FCSTD DOCUMENT  (FreeCAD 1.0R39319 (Git))
Label: ASSEMBLY-CANVAS
License: All rights reserved
LicenseURL: https://en.wikipedia.org/wiki/All_rights_reserved
objects: App::Link×9, Part::FeaturePython×7, App::DocumentObjectGroup×3, PartDesign::CoordinateSystem×2, App::FeaturePython×1, Sketcher::SketchObject×1, App::Part×1
note: 11 computed .brp shape members not serialized (recipe doc carries the construction recipe); baked Part::Feature solids carry a one-line shape summary decoded from their .brp
EXTERNAL_REF file=../Design/PLASTIC-CANVAS/PLASTIC-CANVAS.FCStd obj=LCS_Origin
EXTERNAL_REF file=../Design/PLASTIC-CANVAS/PLASTIC-CANVAS.FCStd obj=Body002
EXTERNAL_REF file=../Design/PLASTIC-CANVAS/PLASTIC-CANVAS.FCStd obj=CircleAxis_1
EXTERNAL_REF file=../Design/RUBBER-FOOT/RUBBER-FOOT.FCStd obj=CircleAxis_2
EXTERNAL_REF file=../Design/RUBBER-FOOT/RUBBER-FOOT.FCStd obj=Body
EXTERNAL_REF file=../Design/INSERT-M1.6x2.5x3/INSERT-M1.6x2.5x3.FCStd obj=CircleAxis_1
EXTERNAL_REF file=../Design/PLASTIC-CANVAS/PLASTIC-CANVAS.FCStd obj=CircleAxis_3
EXTERNAL_REF file=../Design/INSERT-M1.6x2.5x3/INSERT-M1.6x2.5x3.FCStd obj=Body
EXTERNAL_REF file=../Design/INSERT-M1.6x2.5x4/INSERT-M1.6x2.5x4.FCStd obj=Plane_1
EXTERNAL_REF file=../Design/PLASTIC-CANVAS/PLASTIC-CANVAS.FCStd obj=CircleAxis_4
EXTERNAL_REF file=../Design/INSERT-M1.6x2.5x4/INSERT-M1.6x2.5x4.FCStd obj=Body
EXTERNAL_REF file=../Design/MAGNET-D3x14/MAGNET-D3x14.FCStd obj=LCS_1
EXTERNAL_REF file=../Design/PLASTIC-CANVAS/PLASTIC-CANVAS.FCStd obj=LCS_3
EXTERNAL_REF file=../Design/MAGNET-D3x14/MAGNET-D3x14.FCStd obj=Body001
EXTERNAL_REF file=../Design/PLASTIC-CANVAS/PLASTIC-CANVAS.FCStd obj=LCS_4
EXTERNAL_REF file=../Design/MAGNET-SQ3/MAGNET-SQ3.FCStd obj=Axis_2
EXTERNAL_REF file=../Design/PLASTIC-CANVAS/PLASTIC-CANVAS.FCStd obj=Axis_2
EXTERNAL_REF file=../Design/MAGNET-SQ3/MAGNET-SQ3.FCStd obj=Body002
EXTERNAL_REF file=PCBAs/PCBA-INTERFACE.FCStd obj=CircleAxis_1
EXTERNAL_REF file=../Design/PLASTIC-CANVAS/PLASTIC-CANVAS.FCStd obj=Axis_3
EXTERNAL_REF file=PCBAs/PCBA-INTERFACE.FCStd obj=PCBA_INTERFACE_3D_1
EXTERNAL_REF file=../Design/PLASTIC-CANVAS/PLASTIC-CANVAS.FCStd obj=LCS_5
EXTERNAL_REF file=../Design/PLASTIC-MAPMODE/PLASTIC-MAPMODE.FCStd obj=LCS_1
EXTERNAL_REF file=../Design/PLASTIC-MAPMODE/PLASTIC-MAPMODE.FCStd obj=Body

FEATURE [App::DocumentObjectGroup] Parts
FEATURE [PartDesign::CoordinateSystem] LCS_Origin
  AttacherType = Attacher::AttachEngine3D
  AttachmentSupport = -> [X_Axis]
  MapMode = 2
FEATURE [App::DocumentObjectGroup] Constraints
FEATURE [App::FeaturePython] Variables  # WARN: FeaturePython — macro-defined, semantics opaque (R4)
  Type = App::PropertyContainer
FEATURE [App::DocumentObjectGroup] Configurations
FEATURE [App::Link] PLASTIC_CANVAS  label="PLASTIC-CANVAS"
  AttachedBy = #LCS_Origin
  AttachedTo = Parent Assembly#LCS_Origin
  LinkedObject = -> <external ../Design/PLASTIC-CANVAS/PLASTIC-CANVAS.FCStd>#Body002
  SolverId = Asm4EE
  expr: Placement = LCS_Origin.Placement * AttachmentOffset * PLASTIC_CANVAS#LCS_Origin.Placement ^ -1
FEATURE [App::Link] RUBBER_FOOT  label="RUBBER-FOOT"
  AttachedBy = #CircleAxis_2
  AttachedTo = PLASTIC_CANVAS#CircleAxis_1
  LinkPlacement = pos=(-33.85,38,-16) rot=(0,0,1;0rad)
  LinkedObject = -> <external ../Design/RUBBER-FOOT/RUBBER-FOOT.FCStd>#Body
  Placement = pos=(-33.85,38,-16) rot=(0,0,1;0rad)
  SolverId = Asm4EE
  expr: Placement = PLASTIC_CANVAS.Placement * PLASTIC_CANVAS#CircleAxis_1.Placement * AttachmentOffset * RUBBER_FOOT#CircleAxis_2.Placement ^ -1
FEATURE [Part::FeaturePython] Circular_RUBBER_FOOT  label="Circular_RUBBER-FOOT"  # Draft array (typed FeaturePython)
  AngleStep = 90
  ArrayType = Circular Array
  Axis = -> LCS_Origin [Z]
  Count = 4
  Index = 1
  PlacementList = 4 placements: [(-33.85,38,-16),(-38,-33.85,-16),(33.85,-38,-16),(38,33.85,-16)]
  Placer = pos=(0,0,0) rot=(0,0,1;4.71239rad)
  ScaleList = (4) [(1,1,1),(1,1,1),(1,1,1),(1,1,1)]
  Scaler = 1
  ShowElement = false
  SourceObject = -> RUBBER_FOOT
  expr: .Placer.Rotation.Angle = AngleStep * Index
  expr: AngleStep = 360 / Count
FEATURE [App::Link] INSERT_M1_6x2_5x3  label="INSERT-M1.6x2.5x3"
  AttachedBy = #CircleAxis_1
  AttachedTo = PLASTIC_CANVAS#CircleAxis_3
  AttachmentOffset = pos=(0,0,0) rot=(1,0,0;3.14159rad)
  LinkPlacement = pos=(-26.67,26.67,-14) rot=(1,0,0;3.14159rad)
  LinkedObject = -> <external ../Design/INSERT-M1.6x2.5x3/INSERT-M1.6x2.5x3.FCStd>#Body
  Placement = pos=(-26.67,26.67,-14) rot=(1,0,0;3.14159rad)
  SolverId = Asm4EE
  expr: Placement = PLASTIC_CANVAS.Placement * PLASTIC_CANVAS#CircleAxis_3.Placement * AttachmentOffset * INSERT_M1_6x2_5x3#CircleAxis_1.Placement ^ -1
FEATURE [Part::FeaturePython] Circular_INSERT_M1_6x2_5x3  label="Circular_INSERT-M1.6x2.5x3"  # Draft array (typed FeaturePython)
  AngleStep = 90
  ArrayType = Circular Array
  Axis = -> LCS_Origin [Z]
  Count = 4
  Index = 1
  PlacementList = 4 placements: [(-26.67,26.67,-14),(-26.67,-26.67,-14),(26.67,-26.67,-14),(26.67,26.67,-14)]
  Placer = pos=(0,0,0) rot=(0,0,1;4.71239rad)
  ScaleList = (4) [(1,1,1),(1,1,1),(1,1,1),(1,1,1)]
  Scaler = 1
  ShowElement = false
  SourceObject = -> INSERT_M1_6x2_5x3
  expr: .Placer.Rotation.Angle = AngleStep * Index
  expr: AngleStep = 360 / Count
FEATURE [App::Link] INSERT_M1_6x2_5x4  label="INSERT-M1.6x2.5x4"
  AttachedBy = #Plane_1
  AttachedTo = PLASTIC_CANVAS#CircleAxis_4
  AttachmentOffset = pos=(0,0,0) rot=(1,0,0;3.14159rad)
  LinkPlacement = pos=(-50,50,-13.5) rot=(1,0,0;3.14159rad)
  LinkedObject = -> <external ../Design/INSERT-M1.6x2.5x4/INSERT-M1.6x2.5x4.FCStd>#Body
  Placement = pos=(-50,50,-13.5) rot=(1,0,0;3.14159rad)
  SolverId = Asm4EE
  expr: Placement = PLASTIC_CANVAS.Placement * PLASTIC_CANVAS#CircleAxis_4.Placement * AttachmentOffset * INSERT_M1_6x2_5x4#Plane_1.Placement ^ -1
FEATURE [Part::FeaturePython] Circular_INSERT_M1_6x2_5x4  label="Circular_INSERT-M1.6x2.5x4"  # Draft array (typed FeaturePython)
  AngleStep = 90
  ArrayType = Circular Array
  Axis = -> LCS_Origin [Z]
  Count = 4
  Index = 1
  PlacementList = 4 placements: [(-50,50,-13.5),(-50,-50,-13.5),(50,-50,-13.5),(50,50,-13.5)]
  Placer = pos=(0,0,0) rot=(0,0,1;4.71239rad)
  ScaleList = (4) [(1,1,1),(1,1,1),(1,1,1),(1,1,1)]
  Scaler = 1
  ShowElement = false
  SourceObject = -> INSERT_M1_6x2_5x4
  expr: .Placer.Rotation.Angle = AngleStep * Index
  expr: AngleStep = 360 / Count
FEATURE [App::Link] MAGNET_D3x14  label="MAGNET-D3x14"
  AttachedBy = #LCS_1
  AttachedTo = PLASTIC_CANVAS#LCS_3
  AttachmentOffset = pos=(0,0,0.25) rot=(0.71,-0.71,0;3.14159rad)
  LinkPlacement = pos=(-47,51.7,-13.25) rot=(0,0,-1;4.00114rad)
  LinkedObject = -> <external ../Design/MAGNET-D3x14/MAGNET-D3x14.FCStd>#Body001
  Placement = pos=(-47,51.7,-13.25) rot=(0,0,-1;4.00114rad)
  SolverId = Asm4EE
  expr: Placement = PLASTIC_CANVAS.Placement * PLASTIC_CANVAS#LCS_3.Placement * AttachmentOffset * MAGNET_D3x14#LCS_1.Placement ^ -1
FEATURE [App::Link] MAGNET_D3x015  label="MAGNET-D3x015"
  AttachedBy = #LCS_1
  AttachedTo = PLASTIC_CANVAS#LCS_4
  AttachmentOffset = pos=(0,0,0.25) rot=(1,0,0;3.14159rad)
  LinkPlacement = pos=(-51.7,47,-13.25) rot=(0,0,1;2.28204rad)
  LinkedObject = -> <external ../Design/MAGNET-D3x14/MAGNET-D3x14.FCStd>#Body001
  Placement = pos=(-51.7,47,-13.25) rot=(0,0,1;2.28204rad)
  SolverId = Asm4EE
  expr: Placement = PLASTIC_CANVAS.Placement * PLASTIC_CANVAS#LCS_4.Placement * AttachmentOffset * MAGNET_D3x14#LCS_1.Placement ^ -1
FEATURE [Part::FeaturePython] Circular_MAGNET_D3x14  label="Circular_MAGNET-D3x14"  # Draft array (typed FeaturePython)
  AngleStep = 90
  ArrayType = Circular Array
  Axis = -> LCS_Origin [Z]
  Count = 4
  Index = 1
  PlacementList = 4 placements: [(-47,51.7,-13.25),(-51.7,-47,-13.25),(47,-51.7,-13.25),(51.7,47,-13.25)]
  Placer = pos=(0,0,0) rot=(0,0,1;4.71239rad)
  ScaleList = (4) [(1,1,1),(1,1,1),(1,1,1),(1,1,1)]
  Scaler = 1
  ShowElement = false
  SourceObject = -> MAGNET_D3x14
  expr: .Placer.Rotation.Angle = AngleStep * Index
  expr: AngleStep = 360 / Count
FEATURE [Part::FeaturePython] Circular_MAGNET_D3x015  label="Circular_MAGNET-D3x015"  # Draft array (typed FeaturePython)
  AngleStep = 90
  ArrayType = Circular Array
  Axis = -> LCS_Origin [Z]
  Count = 4
  Index = 1
  PlacementList = 4 placements: [(-51.7,47,-13.25),(-47,-51.7,-13.25),(51.7,-47,-13.25),(47,51.7,-13.25)]
  Placer = pos=(0,0,0) rot=(0,0,1;4.71239rad)
  ScaleList = (4) [(1,1,1),(1,1,1),(1,1,1),(1,1,1)]
  Scaler = 1
  ShowElement = false
  SourceObject = -> MAGNET_D3x015
  expr: .Placer.Rotation.Angle = AngleStep * Index
  expr: AngleStep = 360 / Count
FEATURE [App::Link] MAGNET_SQ3  label="MAGNET-SQ3"
  AttachedBy = #Axis_2
  AttachedTo = PLASTIC_CANVAS#Axis_2
  AttachmentOffset = pos=(-0.2,0,16.18) rot=(0,1,0;3.14159rad)
  LinkPlacement = pos=(16.18,50.12,-13.25) rot=(0,0,1;3.14159rad)
  LinkedObject = -> <external ../Design/MAGNET-SQ3/MAGNET-SQ3.FCStd>#Body002
  Placement = pos=(16.18,50.12,-13.25) rot=(0,0,1;3.14159rad)
  SolverId = Asm4EE
  expr: Placement = PLASTIC_CANVAS.Placement * PLASTIC_CANVAS#Axis_2.Placement * AttachmentOffset * MAGNET_SQ3#Axis_2.Placement ^ -1
FEATURE [Part::FeaturePython] Circular_MAGNET_SQ3  label="Circular_MAGNET-SQ3"  # Draft array (typed FeaturePython)
  AngleStep = 90
  ArrayType = Circular Array
  Axis = -> LCS_Origin [Z]
  Count = 4
  Index = 1
  PlacementList = 4 placements: [(16.18,50.12,-13.25),(-50.12,16.18,-13.25),(-16.18,-50.12,-13.25),(50.12,-16.18,-13.25)]
  Placer = pos=(0,0,0) rot=(0,0,1;4.71239rad)
  ScaleList = (4) [(1,1,1),(1,1,1),(1,1,1),(1,1,1)]
  Scaler = 1
  ShowElement = false
  SourceObject = -> MAGNET_SQ3
  expr: .Placer.Rotation.Angle = AngleStep * Index
  expr: AngleStep = 360 / Count
FEATURE [App::Link] PCBA_INTERFACE_3D_1  label="PCBA-INTERFACE-3D 1"
  AttachedBy = #CircleAxis_1
  AttachedTo = PLASTIC_CANVAS#Axis_3
  AttachmentOffset = pos=(0,0,0) rot=(0,0,1.00409;4.71239rad)
  LinkPlacement = pos=(-100.032,53.1114,100.044) rot=(-1,0.000152,-0.000155;4.72984rad)
  LinkedObject = -> <external PCBAs/PCBA-INTERFACE.FCStd>#PCBA_INTERFACE_3D_1
  Placement = pos=(-100.032,53.1114,100.044) rot=(-1,0.000152,-0.000155;4.72984rad)
  SolverId = Asm4EE
  expr: Placement = PLASTIC_CANVAS.Placement * PLASTIC_CANVAS#Axis_3.Placement * AttachmentOffset * PCBA_INTERFACE#CircleAxis_1.Placement ^ -1
FEATURE [Part::FeaturePython] Circular_PCBA_INTERFACE_3D_1  label="Circular_PCBA-INTERFACE-3D 1"  # Draft array (typed FeaturePython)
  AngleStep = 90
  ArrayType = Circular Array
  Axis = -> LCS_Origin [Z]
  Count = 4
  Index = 1
  PlacementList = 4 placements: [(-100.032,53.1114,100.044),(-53.1114,-100.032,100.044),(100.032,-53.1114,100.044),(53.1114,100.032,100.044)]
  Placer = pos=(0,0,0) rot=(0,0,1;4.71239rad)
  ScaleList = (4) [(1,1,1),(1,1,1),(1,1,1),(1,1,1)]
  Scaler = 1
  ShowElement = false
  SourceObject = -> PCBA_INTERFACE_3D_1
  expr: .Placer.Rotation.Angle = AngleStep * Index
  expr: AngleStep = 360 / Count
FEATURE [PartDesign::CoordinateSystem] LCS_1
  AttacherType = Attacher::AttachEngine3D
FEATURE [Sketcher::SketchObject] Sketch_1
  ArcFitTolerance = 1e-06
  AttachmentSupport = -> [XZ_Plane]
  FullyConstrained = true
  MakeInternals = false
  MapMode = 5
  Placement = pos=(0,0,0) rot=(1,0,0;1.5708rad)
FEATURE [App::Link] PLASTIC_MAPMODE  label="PLASTIC-MAPMODE"
  AttachedBy = #LCS_1
  AttachedTo = PLASTIC_CANVAS#LCS_5
  AttachmentOffset = pos=(0,0,0.8) rot=(0,0,1;0rad)
  LinkPlacement = pos=(-2.147e-13,-48.5772,-6.3955) rot=(-0.579059,-0.573917,-0.579059;4.18363rad)
  LinkedObject = -> <external ../Design/PLASTIC-MAPMODE/PLASTIC-MAPMODE.FCStd>#Body
  Placement = pos=(-2.147e-13,-48.5772,-6.3955) rot=(-0.579059,-0.573917,-0.579059;4.18363rad)
  SolverId = Asm4EE
  expr: Placement = PLASTIC_CANVAS.Placement * PLASTIC_CANVAS#LCS_5.Placement * AttachmentOffset * PLASTIC_MAPMODE#LCS_1.Placement ^ -1
FEATURE [App::Part] Assembly
  AssemblyType = Part::Link
  Group = -> [LCS_Origin,Constraints,Variables,Configurations,PLASTIC_CANVAS,RUBBER_FOOT,Circular_RUBBER_FOOT,INSERT_M1_6x2_5x3,Circular_INSERT_M1_6x2_5x3,INSERT_M1_6x2_5x4,Circular_INSERT_M1_6x2_5x4,MAGNET_D3x14,MAGNET_D3x015,Circular_MAGNET_D3x14,Circular_MAGNET_D3x015,MAGNET_SQ3,Circular_MAGNET_SQ3,PCBA_INTERFACE_3D_1,Circular_PCBA_INTERFACE_3D_1,LCS_1,Sketch_1,PLASTIC_MAPMODE]
  Origin = -> Origin
  Type = Assembly

RESOLVED EXTERNAL PARTS (link-assembly join: the EXTERNAL_REF files above that resolve inside this repo's crawl, each included once):
---- part ../Design/INSERT-M1.6x2.5x3/INSERT-M1.6x2.5x3.FCStd = doc fcstd_65dee94a8ec8 ----
FCSTD DOCUMENT  (FreeCAD 1.0R39319 (Git))
Label: INSERT-M1.6x2.5x3
License: All rights reserved
LicenseURL: https://en.wikipedia.org/wiki/All_rights_reserved
objects: Sketcher::SketchObject×4, PartDesign::Pad×2, PartDesign::Plane×2, PartDesign::PolarPattern×1, PartDesign::Groove×1, PartDesign::AdditiveHelix×1, PartDesign::Line×1, PartDesign::Body×1
note: 26 computed .brp shape members not serialized (recipe doc carries the construction recipe); baked Part::Feature solids carry a one-line shape summary decoded from their .brp

FEATURE [Sketcher::SketchObject] Sketch
  ArcFitTolerance = 0
  AttachmentSupport = -> [XY_Plane]
  FullyConstrained = true
  MakeInternals = false
  MapMode = 5
  sketch-geometry (2):
    g0: Circle CenterX=0 CenterY=0 CenterZ=0 NormalX=0 NormalY=0 NormalZ=1 AngleXU=0 Radius=0.8
    g1: Circle CenterX=0 CenterY=0 CenterZ=0 NormalX=0 NormalY=0 NormalZ=1 AngleXU=0 Radius=1
  constraints (4):
    c: Coincident(g0,g-1)
    c: Coincident(g1,g0)
    c: Diameter(g0) = 1.6
    c: Diameter(g1) = 2
FEATURE [PartDesign::Pad] Pad
  Direction = (0,0,1)
  Length = 3
  Length2 = 10
  Midplane = true
  Profile = -> Sketch
  ReferenceAxis = -> Sketch [N_Axis]
  Suppressed = false
  Type = 0
FEATURE [Sketcher::SketchObject] Sketch001
  ArcFitTolerance = 0
  AttachmentSupport = -> [XZ_Plane]
  FullyConstrained = true
  MakeInternals = false
  MapMode = 5
  Placement = pos=(0,0,0) rot=(1,0,0;1.5708rad)
  sketch-geometry (5):
    g0: LineSegment StartX=-0.8 StartY=-1.4 StartZ=0 EndX=-0.6105 EndY=-1.29059 EndZ=0
    g1: LineSegment StartX=-0.6105 StartY=-1.29059 StartZ=0 EndX=-0.8 EndY=-1.18118 EndZ=0
    g2: LineSegment StartX=-0.8 StartY=-1.4 StartZ=0 EndX=-0.9 EndY=-1.4 EndZ=0
    g3: LineSegment StartX=-0.9 StartY=-1.4 StartZ=0 EndX=-0.9 EndY=-1.18118 EndZ=0
    g4: LineSegment StartX=-0.8 StartY=-1.18118 StartZ=0 EndX=-0.9 EndY=-1.18118 EndZ=0
  constraints (15):
    c: Coincident(g1,g0)
    c: Vertical(g0,g1)
    c: Equal(g1,g0)
    c: Angle(g1,g0) = 1.0472
    c: Coincident(g2,g0)
    c: Horizontal(g2)
    c: Coincident(g3,g2)
    c: Vertical(g3)
    c: Coincident(g4,g1)
    c: Horizontal(g4)
    c: Coincident(g3,g4)
    c: Distance(g4) = 0.1
    c: Distance(g0,g-2) = 0.6105
    c: DistanceX(g1,g-1) = 0.8
    c: DistanceY(g0,g-1) = 1.4
FEATURE [PartDesign::Plane] DatumPlane
  AttachmentOffset = pos=(0,0,1.5) rot=(0,0,1;0rad)
  AttachmentSupport = -> [XY_Plane]
  Length = 60
  MapMode = 5
  Placement = pos=(0,0,1.5) rot=(0,0,1;0rad)
  ResizeMode = 0
  Width = 60
FEATURE [Sketcher::SketchObject] Sketch002
  ArcFitTolerance = 0
  AttachmentSupport = -> [DatumPlane]
  FullyConstrained = true
  MakeInternals = false
  MapMode = 5
  Placement = pos=(0,0,1.5) rot=(0,0,1;0rad)
  sketch-geometry (2):
    g0: ArcOfCircle CenterX=0 CenterY=0 CenterZ=0 NormalX=0 NormalY=0 NormalZ=1 AngleXU=0 Radius=0.85 StartAngle=1.35344 EndAngle=1.78815
    g1: ArcOfCircle CenterX=0 CenterY=1 CenterZ=0 NormalX=0 NormalY=0 NormalZ=1 AngleXU=0 Radius=0.25 StartAngle=5.53542 EndAngle=10.1725
  constraints (7):
    c: Diameter(g0) = 1.7
    c: PointOnObject(g1,g-2)
    c: Diameter(g1) = 0.5
    c: Coincident(g0,g1)
    c: Coincident(g0,g1)
    c: DistanceY(g0,g1) = 1
    c: Coincident(g0,g-1)
FEATURE [PartDesign::Pad] Pad001
  BaseFeature = -> Pad
  Direction = (0,0,1)
  Length = 3
  Length2 = 10
  Profile = -> Sketch002
  ReferenceAxis = -> Sketch002 [N_Axis]
  Refine = true
  Reversed = true
  Suppressed = false
  Type = 0
FEATURE [PartDesign::PolarPattern] PolarPattern
  Angle = 360
  Axis = -> Sketch002 [N_Axis]
  BaseFeature = -> Pad001
  Mode = 0
  Occurrences = 21
  Offset = 120
  Originals = -> [Pad001]
  Refine = true
  Suppressed = false
  TransformMode = 0
FEATURE [Sketcher::SketchObject] Sketch003
  ArcFitTolerance = 0
  AttachmentSupport = -> [XZ_Plane]
  FullyConstrained = true
  MakeInternals = false
  MapMode = 5
  Placement = pos=(0,0,0) rot=(1,0,0;1.5708rad)
  sketch-geometry (5):
    g0: LineSegment StartX=-1 StartY=0.5 StartZ=0 EndX=-1 EndY=-0.5 EndZ=0
    g1: LineSegment [constr] StartX=0 StartY=0 StartZ=0 EndX=-1 EndY=0 EndZ=0
    g2: LineSegment StartX=-1 StartY=0.5 StartZ=0 EndX=-1.6 EndY=0.5 EndZ=0
    g3: LineSegment StartX=-1.6 StartY=0.5 StartZ=0 EndX=-1.6 EndY=-0.5 EndZ=0
    g4: LineSegment StartX=-1 StartY=-0.5 StartZ=0 EndX=-1.6 EndY=-0.5 EndZ=0
  constraints (14):
    c: Coincident(g1,g-1)
    c: Horizontal(g1)
    c: Symmetric(g0,g0,g1)
    c: DistanceY(g0,g0) = 1
    c: Coincident(g2,g0)
    c: Horizontal(g2)
    c: Coincident(g3,g2)
    c: Vertical(g3)
    c: Coincident(g4,g0)
    c: Horizontal(g4)
    c: Coincident(g3,g4)
    c: DistanceX(g2,g2) = 0.6
    c: Vertical(g0)
    c: DistanceX(g1,g1) = 1
FEATURE [PartDesign::Groove] Groove
  Angle = 360
  Angle2 = 60
  Axis = (0,2e-16,1)
  Base = (0,0,0)
  BaseFeature = -> PolarPattern
  Profile = -> Sketch003
  ReferenceAxis = -> Sketch003 [V_Axis]
  Reversed = true
  Suppressed = false
  Type = 0
FEATURE [PartDesign::AdditiveHelix] AdditiveHelix
  Angle = 0
  Axis = (0,2e-16,1)
  Base = (0,0,0)
  BaseFeature = -> Groove
  Growth = 0
  HasBeenEdited = true
  Height = 2.6
  LeftHanded = false
  Mode = 0
  Outside = false
  Pitch = 0.35
  Profile = -> Sketch001
  ReferenceAxis = -> Sketch001 [V_Axis]
  Refine = true
  Suppressed = false
  Tolerance = 0.1
  Turns = 7.42857
FEATURE [PartDesign::Plane] Plane_1
  AttachmentSupport = -> [AdditiveHelix]
  Length = 100
  MapMode = 5
  Placement = pos=(0,0,1.5) rot=(0,0,1;0rad)
  ResizeMode = 1
  Width = 100
FEATURE [PartDesign::Line] CircleAxis_1
  AttacherType = Attacher::AttachEngineLine
  AttachmentSupport = -> [AdditiveHelix]
  Length = 4.50902
  MapMode = 19
  Placement = pos=(-1e-16,0,1.5) rot=(0,0,1;0rad)
  ResizeMode = 1
FEATURE [PartDesign::Body] Body  label="INSERT-M1.6x2.5x3"
  AllowCompound = false
  Group = -> [Sketch,Pad,Sketch001,DatumPlane,Sketch002,Pad001,PolarPattern,Sketch003,Groove,AdditiveHelix,Plane_1,CircleAxis_1]
  Origin = -> Origin
  Tip = -> AdditiveHelix
---- part ../Design/INSERT-M1.6x2.5x4/INSERT-M1.6x2.5x4.FCStd = doc fcstd_df083e575286 ----
FCSTD DOCUMENT  (FreeCAD 1.0R39319 (Git))
Label: INSERT-M1.6x2.5x4
License: All rights reserved
LicenseURL: https://en.wikipedia.org/wiki/All_rights_reserved
objects: Sketcher::SketchObject×4, PartDesign::Pad×2, PartDesign::Plane×2, PartDesign::AdditiveHelix×1, PartDesign::PolarPattern×1, PartDesign::Groove×1, PartDesign::Line×1, PartDesign::Body×1
note: 26 computed .brp shape members not serialized (recipe doc carries the construction recipe); baked Part::Feature solids carry a one-line shape summary decoded from their .brp

FEATURE [Sketcher::SketchObject] Sketch
  ArcFitTolerance = 0
  AttachmentSupport = -> [XY_Plane]
  FullyConstrained = true
  MakeInternals = false
  MapMode = 5
  sketch-geometry (2):
    g0: Circle CenterX=0 CenterY=0 CenterZ=0 NormalX=0 NormalY=0 NormalZ=1 AngleXU=0 Radius=0.8
    g1: Circle CenterX=0 CenterY=0 CenterZ=0 NormalX=0 NormalY=0 NormalZ=1 AngleXU=0 Radius=1
  constraints (4):
    c: Coincident(g0,g-1)
    c: Coincident(g1,g0)
    c: Diameter(g0) = 1.6
    c: Diameter(g1) = 2
FEATURE [PartDesign::Pad] Pad
  Direction = (0,0,1)
  Length = 4
  Length2 = 10
  Midplane = true
  Profile = -> Sketch
  ReferenceAxis = -> Sketch [N_Axis]
  Suppressed = false
  Type = 0
FEATURE [Sketcher::SketchObject] Sketch001
  ArcFitTolerance = 0
  AttachmentSupport = -> [XZ_Plane]
  ExternalGeometry = -> [Pad]
  FullyConstrained = true
  MakeInternals = false
  MapMode = 5
  Placement = pos=(0,0,0) rot=(1,0,0;1.5708rad)
  sketch-geometry (5):
    g0: LineSegment StartX=-0.8 StartY=-2 StartZ=0 EndX=-0.6105 EndY=-1.89059 EndZ=0
    g1: LineSegment StartX=-0.6105 StartY=-1.89059 StartZ=0 EndX=-0.8 EndY=-1.78118 EndZ=0
    g2: LineSegment StartX=-0.8 StartY=-2 StartZ=0 EndX=-0.9 EndY=-2 EndZ=0
    g3: LineSegment StartX=-0.9 StartY=-2 StartZ=0 EndX=-0.9 EndY=-1.78118 EndZ=0
    g4: LineSegment StartX=-0.8 StartY=-1.78118 StartZ=0 EndX=-0.9 EndY=-1.78118 EndZ=0
  constraints (14):
    c: Coincident(g0,g-3)
    c: Coincident(g1,g0)
    c: Vertical(g0,g1)
    c: Equal(g1,g0)
    c: Angle(g1,g0) = 1.0472
    c: Coincident(g2,g0)
    c: Horizontal(g2)
    c: Coincident(g3,g2)
    c: Vertical(g3)
    c: Coincident(g4,g1)
    c: Horizontal(g4)
    c: Coincident(g3,g4)
    c: Distance(g4) = 0.1
    c: Distance(g0,g-2) = 0.6105
FEATURE [PartDesign::AdditiveHelix] AdditiveHelix
  Angle = 0
  Axis = (0,2e-16,1)
  Base = (0,0,0)
  BaseFeature = -> Pad
  Growth = 0
  HasBeenEdited = true
  Height = 3.7
  LeftHanded = false
  Mode = 0
  Outside = false
  Pitch = 0.35
  Profile = -> Sketch001
  ReferenceAxis = -> Sketch001 [V_Axis]
  Suppressed = false
  Tolerance = 0.1
  Turns = 10.5714
FEATURE [PartDesign::Plane] DatumPlane
  AttachmentSupport = -> [AdditiveHelix]
  Length = 60
  MapMode = 5
  Placement = pos=(0,0,2) rot=(0,0,1;0rad)
  ResizeMode = 0
  Width = 60
FEATURE [Sketcher::SketchObject] Sketch002
  ArcFitTolerance = 0
  AttachmentSupport = -> [DatumPlane]
  ExternalGeometry = -> [AdditiveHelix]
  FullyConstrained = true
  MakeInternals = false
  MapMode = 5
  Placement = pos=(0,0,2) rot=(0,0,1;0rad)
  sketch-geometry (2):
    g0: ArcOfCircle CenterX=0 CenterY=0 CenterZ=0 NormalX=0 NormalY=0 NormalZ=1 AngleXU=0 Radius=0.925 StartAngle=1.32219 EndAngle=1.8194
    g1: ArcOfCircle CenterX=0 CenterY=1 CenterZ=0 NormalX=0 NormalY=0 NormalZ=1 AngleXU=0 Radius=0.25 StartAngle=5.85662 EndAngle=9.85135
  constraints (7):
    c: Coincident(g0,g-3)
    c: Diameter(g0) = 1.85
    c: PointOnObject(g1,g-2)
    c: PointOnObject(g1,g-3)
    c: Diameter(g1) = 0.5
    c: Coincident(g0,g1)
    c: Coincident(g0,g1)
FEATURE [PartDesign::Pad] Pad001
  BaseFeature = -> AdditiveHelix
  Direction = (0,0,1)
  Length = 4
  Length2 = 10
  Profile = -> Sketch002
  ReferenceAxis = -> Sketch002 [N_Axis]
  Refine = true
  Reversed = true
  Suppressed = false
  Type = 0
FEATURE [PartDesign::PolarPattern] PolarPattern
  Angle = 360
  Axis = -> Sketch002 [N_Axis]
  BaseFeature = -> Pad001
  Mode = 0
  Occurrences = 21
  Offset = 120
  Originals = -> [Pad001]
  Refine = true
  Suppressed = false
  TransformMode = 0
FEATURE [Sketcher::SketchObject] Sketch003
  ArcFitTolerance = 0
  AttachmentSupport = -> [XZ_Plane]
  FullyConstrained = true
  MakeInternals = false
  MapMode = 5
  Placement = pos=(0,0,0) rot=(1,0,0;1.5708rad)
  sketch-geometry (5):
    g0: LineSegment StartX=-1 StartY=1 StartZ=0 EndX=-1 EndY=-1 EndZ=0
    g1: LineSegment [constr] StartX=0 StartY=0 StartZ=0 EndX=-1 EndY=0 EndZ=0
    g2: LineSegment StartX=-1 StartY=1 StartZ=0 EndX=-1.6 EndY=1 EndZ=0
    g3: LineSegment StartX=-1.6 StartY=1 StartZ=0 EndX=-1.6 EndY=-1 EndZ=0
    g4: LineSegment StartX=-1 StartY=-1 StartZ=0 EndX=-1.6 EndY=-1 EndZ=0
  constraints (14):
    c: Coincident(g1,g-1)
    c: Horizontal(g1)
    c: Symmetric(g0,g0,g1)
    c: DistanceY(g0,g0) = 2
    c: Coincident(g2,g0)
    c: Horizontal(g2)
    c: Coincident(g3,g2)
    c: Vertical(g3)
    c: Coincident(g4,g0)
    c: Horizontal(g4)
    c: Coincident(g3,g4)
    c: DistanceX(g2,g2) = 0.6
    c: Vertical(g0)
    c: DistanceX(g1,g1) = 1
FEATURE [PartDesign::Groove] Groove
  Angle = 360
  Angle2 = 60
  Axis = (0,2e-16,1)
  Base = (0,0,0)
  BaseFeature = -> PolarPattern
  Profile = -> Sketch003
  ReferenceAxis = -> Sketch003 [V_Axis]
  Refine = true
  Reversed = true
  Suppressed = false
  Type = 0
FEATURE [PartDesign::Plane] Plane_1
  AttachmentSupport = -> [Groove]
  Length = 100
  MapMode = 5
  Placement = pos=(0,0,2) rot=(0,0,1;0rad)
  ResizeMode = 1
  Width = 100
FEATURE [PartDesign::Line] Axis_1
  AttacherType = Attacher::AttachEngineLine
  Length = 200
  ResizeMode = 1
FEATURE [PartDesign::Body] Body  label="INSERT-M1.6x2.5x4"
  AllowCompound = false
  Group = -> [Sketch,Pad,Sketch001,AdditiveHelix,DatumPlane,Sketch002,Pad001,PolarPattern,Sketch003,Groove,Plane_1,Axis_1]
  Origin = -> Origin
  Tip = -> Groove
---- part ../Design/MAGNET-D3x14/MAGNET-D3x14.FCStd = doc fcstd_6cb95a583107 ----
FCSTD DOCUMENT  (FreeCAD 1.0R39319 (Git))
Label: MAGNET-D3x14
License: All rights reserved
LicenseURL: http://en.wikipedia.org/wiki/All_rights_reserved
objects: TechDraw::DrawGeomHatch×4, TechDraw::DrawProjGroupItem×3, TechDraw::DrawViewDimension×2, TechDraw::DrawViewBalloon×2, Sketcher::SketchObject×1, PartDesign::Pad×1, TechDraw::DrawViewAnnotation×1, PartDesign::Mirrored×1, TechDraw::DrawSVGTemplate×1, PartDesign::Plane×1, PartDesign::Line×1, PartDesign::Body×1, TechDraw::DrawProjGroup×1, TechDraw::DrawPage×1
note: 12 computed .brp shape members not serialized (recipe doc carries the construction recipe); baked Part::Feature solids carry a one-line shape summary decoded from their .brp

FEATURE [Sketcher::SketchObject] Sketch001
  ArcFitTolerance = 0
  AttachmentSupport = -> [XY_Plane001]
  FullyConstrained = true
  MakeInternals = false
  MapMode = 5
  sketch-geometry (2):
    g0: ArcOfCircle CenterX=0 CenterY=0 CenterZ=0 NormalX=0 NormalY=0 NormalZ=1 AngleXU=0 Radius=1.45 StartAngle=1.5708 EndAngle=4.71239
    g1: LineSegment StartX=0 StartY=-1.45 StartZ=0 EndX=1e-16 EndY=1.45 EndZ=0
  constraints (6):
    c: Coincident(g0,g-1)
    c: PointOnObject(g0,g-2)
    c: PointOnObject(g0,g-2)
    c: Radius(g0) = 1.45
    c: Coincident(g1,g0)
    c: Coincident(g1,g0)
FEATURE [PartDesign::Pad] Pad001  label="RodN"
  AllowMultiFace = false
  Direction = (0,0,1)
  Length = 14.2
  Length2 = 100
  Profile = -> Sketch001
  ReferenceAxis = -> Sketch001 [N_Axis]
  Refine = true
  Suppressed = false
  Type = 0
FEATURE [TechDraw::DrawViewAnnotation] Annotation
  Font = osifont
  LineSpace = 80
  LockPosition = false
  MaxWidth = -1
  Rotation = 0
  Scale = 3
  ScaleType = 0
  Text = Minimum Magnet Grade: N52
  TextSize = 5
  TextStyle = 0
  X = 87.2293
  Y = 185.906
FEATURE [PartDesign::Mirrored] Mirrored
  BaseFeature = -> Pad001
  MirrorPlane = -> Sketch001 [V_Axis]
  Originals = -> [Pad001]
  Suppressed = false
  TransformMode = 0
FEATURE [TechDraw::DrawSVGTemplate] Template
  EditableTexts = Designed_by_Name=Designed by Name; Drawing_number=Drawing number; FC-Date=2025.06.23.; FC-SC=Scale; FC-SH=Sheet; FC-Title=Title; Subtitle=Subtitle; Weight=Weight
  Height = 210
  Orientation = 1
  Template = /snap/freecad/759/usr/share/Mod/TechDraw/Templates/A4_LandscapeTD.svg
  Width = 297
FEATURE [PartDesign::Plane] Plane_1
  AttachmentSupport = -> [Mirrored]
  Length = 100
  MapMode = 5
  Placement = pos=(0,0,14.2) rot=(0,0,1;0rad)
  ResizeMode = 1
  Width = 100
FEATURE [PartDesign::Line] Axis_1
  AttacherType = Attacher::AttachEngineLine
  Length = 200
  ResizeMode = 1
FEATURE [PartDesign::Body] Body001  label="MAGNET-D3x14"
  AllowCompound = false
  Group = -> [Sketch001,Pad001,Mirrored,Plane_1,Axis_1]
  Origin = -> Origin001
  Placement = pos=(0,0,0) rot=(0,0,1;3.14159rad)
  Tip = -> Mirrored
FEATURE [TechDraw::DrawProjGroupItem] ProjItem  label="Front"
  CoarseView = false
  Direction = (0,-1,0)
  Focus = 100
  HardHidden = false
  IsoCount = 0
  IsoHidden = false
  IsoVisible = false
  LockPosition = true
  Perspective = false
  Rotation = 0
  RotationVector = (1,0,0)
  ScaleType = 2
  ScrubCount = 0
  SeamHidden = false
  SeamVisible = false
  SmoothHidden = false
  SmoothVisible = true
  Source = -> [Body001]
  Type = 0
  X = 0
  XDirection = (1,0,0)
  Y = 0
FEATURE [TechDraw::DrawProjGroupItem] ProjItem012  label="Left001"
  CoarseView = false
  Direction = (-1,-1e-16,0)
  Focus = 100
  HardHidden = false
  IsoCount = 0
  IsoHidden = false
  IsoVisible = false
  LockPosition = false
  Perspective = false
  Rotation = 0
  RotationVector = (1,0,0)
  ScaleType = 2
  ScrubCount = 0
  SeamHidden = false
  SeamVisible = false
  SmoothHidden = false
  SmoothVisible = true
  Source = -> [Body001]
  Type = 1
  X = 38.7
  XDirection = (1e-16,-1,0)
  Y = 0
FEATURE [TechDraw::DrawProjGroupItem] ProjItem013  label="FrontBottomLeft001"
  CoarseView = false
  Direction = (-0.57735,-0.57735,-0.57735)
  Focus = 100
  HardHidden = false
  IsoCount = 0
  IsoHidden = false
  IsoVisible = false
  LockPosition = false
  Perspective = false
  Rotation = 0
  RotationVector = (1,0,0)
  ScaleType = 2
  ScrubCount = 0
  SeamHidden = false
  SeamVisible = false
  SmoothHidden = false
  SmoothVisible = true
  Source = -> [Body001]
  Type = 8
  X = 38.7
  XDirection = (0.707107,-0.707107,0)
  Y = 71.2029
FEATURE [TechDraw::DrawProjGroup] ProjGroup
  Anchor = -> ProjItem
  AutoDistribute = true
  LockPosition = false
  ProjectionType = 0
  Rotation = 0
  Scale = 3
  ScaleType = 0
  Source = -> [Body001]
  Views = -> [ProjItem,ProjItem012,ProjItem013]
  X = 50
  Y = 75
  spacingX = 30
  spacingY = 30
FEATURE [TechDraw::DrawViewDimension] Dimension003
  AngleOverride = false
  Arbitrary = false
  ArbitraryTolerances = false
  EqualTolerance = true
  ExtensionAngle = 0
  FormatSpec = %.2w
  FormatSpecOverTolerance = %+.2w
  FormatSpecUnderTolerance = %+.2w
  Inverted = false
  LineAngle = 0
  LockPosition = false
  MeasureType = 1
  OverTolerance = 0
  References2D = -> [ProjItem]
  Rotation = 0
  Scale = 3
  ScaleType = 0
  TheoreticalExact = false
  Type = 2
  UnderTolerance = 0
  X = -18.0773
  Y = 1.76609
FEATURE [TechDraw::DrawViewDimension] Dimension004
  AngleOverride = false
  Arbitrary = false
  ArbitraryTolerances = false
  EqualTolerance = true
  ExtensionAngle = 0
  FormatSpec = ⌀%.2w
  FormatSpecOverTolerance = %+.2w
  FormatSpecUnderTolerance = %+.2w
  Inverted = false
  LineAngle = 0
  LockPosition = false
  MeasureType = 1
  OverTolerance = 0
  References2D = -> [ProjItem012]
  Rotation = 0
  Scale = 3
  ScaleType = 0
  TheoreticalExact = false
  Type = 1
  UnderTolerance = 0
  X = -14.3762
  Y = 33.435
FEATURE [TechDraw::DrawViewBalloon] Balloon002
  BubbleShape = 6
  EndType = 1
  EndTypeScale = 1
  KinkLength = 5
  LockPosition = false
  OriginX = -2.03
  OriginY = 1.13805
  Rotation = 0
  Scale = 3
  ScaleType = 0
  ShapeScale = 1
  SourceView = -> ProjItem013
  Text = North
  TextWrapLen = -1
  X = -10.3087
  Y = 3.48898
FEATURE [TechDraw::DrawViewBalloon] Balloon003
  BubbleShape = 6
  EndType = 1
  EndTypeScale = 1
  KinkLength = 5
  LockPosition = false
  OriginX = 2.24
  OriginY = -1.72306
  Rotation = 0
  Scale = 3
  ScaleType = 0
  ShapeScale = 1
  SourceView = -> ProjItem013
  Text = South
  TextWrapLen = -1
  X = 12.1747
  Y = -5.18693
FEATURE [TechDraw::DrawPage] Page  label="MAGNET-D3x14_Drawing"
  KeepUpdated = true
  NextBalloonIndex = 5
  ProjectionType = 0
  Scale = 3
  Template = -> Template
  Views = -> [Annotation,ProjGroup,Dimension003,Dimension004,Balloon002,Balloon003]
FEATURE [TechDraw::DrawGeomHatch] GeomHatch
  FilePattern = /snap/freecad/1248/usr/share/Mod/TechDraw/PAT/FCPAT.pat
  NamePattern = Diamond
  PatternOffset = (0,0,0)
  PatternRotation = 0
  ScalePattern = 1
  Source = -> ProjItem013 [Face1]
FEATURE [TechDraw::DrawGeomHatch] GeomHatch001
  FilePattern = /snap/freecad/1248/usr/share/Mod/TechDraw/PAT/FCPAT.pat
  NamePattern = Diamond
  PatternOffset = (0,0,0)
  PatternRotation = 0
  ScalePattern = 1
  Source = -> ProjItem013 [Face4]
FEATURE [TechDraw::DrawGeomHatch] GeomHatch002
  FilePattern = /snap/freecad/1248/usr/share/Mod/TechDraw/PAT/FCPAT.pat
  NamePattern = Diamond
  PatternOffset = (0,0,0)
  PatternRotation = 0
  ScalePattern = 1
  Source = -> ProjItem013 [Face3]
FEATURE [TechDraw::DrawGeomHatch] GeomHatch003
  FilePattern = /snap/freecad/1248/usr/share/Mod/TechDraw/PAT/FCPAT.pat
  NamePattern = Diamond
  PatternOffset = (0,0,0)
  PatternRotation = 0
  ScalePattern = 1
  Source = -> ProjItem013 [Face2]
---- part ../Design/MAGNET-SQ3/MAGNET-SQ3.FCStd = doc fcstd_c496fe24e4ad ----
FCSTD DOCUMENT  (FreeCAD 1.0R39319 (Git))
Label: MAGNET-SQ3
License: All rights reserved
LicenseURL: http://en.wikipedia.org/wiki/All_rights_reserved
objects: TechDraw::DrawProjGroupItem×3, TechDraw::DrawViewDimension×3, PartDesign::Plane×2, TechDraw::DrawGeomHatch×2, TechDraw::DrawViewBalloon×2, TechDraw::DrawViewAnnotation×1, Sketcher::SketchObject×1, PartDesign::Pad×1, PartDesign::Mirrored×1, TechDraw::DrawSVGTemplate×1, PartDesign::Line×1, PartDesign::Body×1, TechDraw::DrawProjGroup×1, TechDraw::DrawPage×1
note: 15 computed .brp shape members not serialized (recipe doc carries the construction recipe); baked Part::Feature solids carry a one-line shape summary decoded from their .brp

FEATURE [TechDraw::DrawViewAnnotation] Annotation004
  Font = osifont
  LineSpace = 80
  LockPosition = false
  MaxWidth = -1
  Rotation = 0
  ScaleType = 1
  Text = Minimum Magnet Grade: N52
  TextSize = 5
  TextStyle = 0
  X = 106.281
  Y = 175.798
FEATURE [Sketcher::SketchObject] Sketch002
  ArcFitTolerance = 0
  AttachmentSupport = -> [XY_Plane003]
  FullyConstrained = true
  MakeInternals = false
  MapMode = 5
  sketch-geometry (6):
    g0: LineSegment StartX=1.5 StartY=1.5 StartZ=0 EndX=0 EndY=1.5 EndZ=0
    g1: LineSegment StartX=0 StartY=1.5 StartZ=0 EndX=0 EndY=-1.5 EndZ=0
    g2: LineSegment StartX=0 StartY=-1.5 StartZ=0 EndX=1.5 EndY=-1.5 EndZ=0
    g3: LineSegment StartX=1.5 StartY=-1.5 StartZ=0 EndX=1.5 EndY=1.5 EndZ=0
    g4: LineSegment [constr] StartX=0 StartY=0 StartZ=0 EndX=1.5 EndY=1.5 EndZ=0
    g5: LineSegment [constr] StartX=1.5 StartY=-1.5 StartZ=0 EndX=0 EndY=0 EndZ=0
  constraints (16):
    c: Coincident(g0,g1)
    c: Coincident(g1,g2)
    c: Coincident(g2,g3)
    c: Coincident(g3,g0)
    c: Horizontal(g0)
    c: Horizontal(g2)
    c: Vertical(g1)
    c: Vertical(g3)
    c: PointOnObject(g1,g-2)
    c: DistanceY(g3,g3) = 3
    c: Coincident(g4,g-1)
    c: Coincident(g4,g0)
    c: Coincident(g5,g2)
    c: Coincident(g5,g4)
    c: Equal(g5,g4)
    c: DistanceX(g0,g0) = 1.5
FEATURE [PartDesign::Pad] Pad002  label="CubeN"
  Direction = (0,0,1)
  Length = 3
  Length2 = 10
  Profile = -> Sketch002
  ReferenceAxis = -> Sketch002 [N_Axis]
  Suppressed = false
  Type = 0
FEATURE [PartDesign::Mirrored] Mirrored001
  BaseFeature = -> Pad002
  MirrorPlane = -> Sketch002 [V_Axis]
  Originals = -> [Pad002]
  Suppressed = false
  TransformMode = 0
FEATURE [TechDraw::DrawSVGTemplate] Template001
  EditableTexts = Designed_by_Name=Designed by Name; Drawing_number=Drawing number; FC-Date=Date; FC-SC=Scale; FC-SH=Sheet; FC-Title=Title; Subtitle=Subtitle; Weight=Weight
  Height = 210
  Orientation = 1
  Template = /snap/freecad/759/usr/share/Mod/TechDraw/Templates/A4_LandscapeTD.svg
  Width = 297
FEATURE [PartDesign::Plane] Plane_1
  Length = 100
  ResizeMode = 1
  Width = 100
FEATURE [PartDesign::Plane] Plane_2
  AttachmentSupport = -> [Mirrored001]
  Length = 100
  MapMode = 5
  Placement = pos=(0,1.5,0) rot=(0,0.707107,0.707107;3.14159rad)
  ResizeMode = 1
  Width = 100
FEATURE [PartDesign::Line] Axis_2
  AttacherType = Attacher::AttachEngineLine
  AttachmentSupport = -> [Mirrored001]
  Length = 200
  MapMode = 29
  Placement = pos=(0,1.5,0) rot=(0.57735,0.57735,0.57735;2.0944rad)
  ResizeMode = 1
FEATURE [PartDesign::Body] Body002  label="MAGNET-SQ3"
  AllowCompound = false
  Group = -> [Sketch002,Pad002,Mirrored001,Plane_1,Plane_2,Axis_2]
  Origin = -> Origin003
  Tip = -> Mirrored001
FEATURE [TechDraw::DrawProjGroupItem] ProjItem009  label="Front001"
  CoarseView = false
  Direction = (0,-1,0)
  Focus = 100
  HardHidden = false
  IsoCount = 0
  IsoHidden = false
  IsoVisible = false
  LockPosition = true
  Perspective = false
  Rotation = 0
  RotationVector = (1,0,0)
  ScaleType = 2
  ScrubCount = 0
  SeamHidden = false
  SeamVisible = false
  SmoothHidden = false
  SmoothVisible = true
  Source = -> [Body002]
  Type = 0
  X = 0
  XDirection = (1,0,0)
  Y = 0
FEATURE [TechDraw::DrawProjGroupItem] ProjItem010  label="Left"
  CoarseView = false
  Direction = (-1,-1e-16,0)
  Focus = 100
  HardHidden = false
  IsoCount = 0
  IsoHidden = false
  IsoVisible = false
  LockPosition = false
  Perspective = false
  Rotation = 0
  RotationVector = (1,0,0)
  ScaleType = 2
  ScrubCount = 0
  SeamHidden = false
  SeamVisible = false
  SmoothHidden = false
  SmoothVisible = true
  Source = -> [Body002]
  Type = 1
  X = 48.1066
  XDirection = (1e-16,-1,0)
  Y = 0
FEATURE [TechDraw::DrawProjGroupItem] ProjItem011  label="FrontBottomLeft"
  CoarseView = false
  Direction = (-0.57735,-0.57735,-0.57735)
  Focus = 100
  HardHidden = false
  IsoCount = 0
  IsoHidden = false
  IsoVisible = false
  LockPosition = false
  Perspective = false
  Rotation = 0
  RotationVector = (1,0,0)
  ScaleType = 2
  ScrubCount = 0
  SeamHidden = false
  SeamVisible = false
  SmoothHidden = false
  SmoothVisible = true
  Source = -> [Body002]
  Type = 8
  X = 48.1066
  XDirection = (0.707107,-0.707107,0)
  Y = 49.7474
FEATURE [TechDraw::DrawProjGroup] ProjGroup001
  Anchor = -> ProjItem009
  AutoDistribute = true
  LockPosition = false
  ProjectionType = 0
  Rotation = 0
  Scale = 5
  ScaleType = 0
  Source = -> [Body002]
  Views = -> [ProjItem009,ProjItem010,ProjItem011]
  X = 50
  Y = 75
  spacingX = 30
  spacingY = 30
FEATURE [TechDraw::DrawGeomHatch] GeomHatch  label="GeomHatchFX1"
  FilePattern = /snap/freecad/759/usr/share/Mod/TechDraw/PAT/FCPAT.pat
  NamePattern = Diamond
  PatternOffset = (0,0,0)
  PatternRotation = 0
  ScalePattern = 1
  Source = -> ProjItem011 [Face1,Face4,Face3]
FEATURE [TechDraw::DrawGeomHatch] GeomHatch001  label="GeomHatch001FX2"
  FilePattern = /snap/freecad/759/usr/share/Mod/TechDraw/PAT/FCPAT.pat
  NamePattern = Diamond
  PatternOffset = (0,0,0)
  PatternRotation = 0
  ScalePattern = 1
  Source = -> ProjItem011 [Face2,Face5]
FEATURE [TechDraw::DrawViewDimension] Dimension
  AngleOverride = false
  Arbitrary = false
  ArbitraryTolerances = false
  EqualTolerance = true
  ExtensionAngle = 0
  FormatSpec = %.2w
  FormatSpecOverTolerance = %+.2w
  FormatSpecUnderTolerance = %+.2w
  Inverted = false
  LineAngle = 0
  LockPosition = false
  MeasureType = 1
  OverTolerance = 0
  References2D = -> [ProjItem009]
  Rotation = 0
  Scale = 5
  ScaleType = 0
  TheoreticalExact = false
  Type = 1
  UnderTolerance = 0
  X = -0.179028
  Y = 26.2916
FEATURE [TechDraw::DrawViewDimension] Dimension001
  AngleOverride = false
  Arbitrary = false
  ArbitraryTolerances = false
  EqualTolerance = true
  ExtensionAngle = 0
  FormatSpec = %.2w
  FormatSpecOverTolerance = %+.2w
  FormatSpecUnderTolerance = %+.2w
  Inverted = false
  LineAngle = 0
  LockPosition = false
  MeasureType = 1
  OverTolerance = 0
  References2D = -> [ProjItem009]
  Rotation = 0
  Scale = 5
  ScaleType = 0
  TheoreticalExact = false
  Type = 2
  UnderTolerance = 0
  X = -21.1061
  Y = 1.96292
FEATURE [TechDraw::DrawViewDimension] Dimension002
  AngleOverride = false
  Arbitrary = false
  ArbitraryTolerances = false
  EqualTolerance = true
  ExtensionAngle = 0
  FormatSpec = %.2w
  FormatSpecOverTolerance = %+.2w
  FormatSpecUnderTolerance = %+.2w
  Inverted = false
  LineAngle = 0
  LockPosition = false
  MeasureType = 1
  OverTolerance = 0
  References2D = -> [ProjItem010]
  Rotation = 0
  Scale = 5
  ScaleType = 0
  TheoreticalExact = false
  Type = 1
  UnderTolerance = 0
  X = 0
  Y = 25.5754
FEATURE [TechDraw::DrawViewBalloon] Balloon
  BubbleShape = 6
  EndType = 1
  EndTypeScale = 1
  KinkLength = 5
  LockPosition = false
  OriginX = -2.9
  OriginY = 2
  Rotation = 0
  Scale = 5
  ScaleType = 0
  ShapeScale = 1
  SourceView = -> ProjItem011
  Text = North
  TextWrapLen = -1
  X = -6.66991
  Y = 2.71803
FEATURE [TechDraw::DrawViewBalloon] Balloon001
  BubbleShape = 6
  EndType = 1
  EndTypeScale = 1
  KinkLength = 5
  LockPosition = false
  OriginX = 3
  OriginY = -1.78
  Rotation = 0
  Scale = 5
  ScaleType = 0
  ShapeScale = 1
  SourceView = -> ProjItem011
  Text = South
  TextWrapLen = -1
  X = 6.86461
  Y = -2.29476
FEATURE [TechDraw::DrawPage] Page001  label="MAGNET-SQ3_Drawing"
  KeepUpdated = true
  NextBalloonIndex = 5
  ProjectionType = 0
  Scale = 5
  Template = -> Template001
  Views = -> [Annotation004,ProjGroup001,Dimension,Dimension001,Dimension002,Balloon,Balloon001]
---- part ../Design/PLASTIC-CANVAS/PLASTIC-CANVAS.FCStd = doc fcstd_c03126f3cfb4 (155221 chars; too large to inline — full recipe in that document) ----
---- part ../Design/PLASTIC-MAPMODE/PLASTIC-MAPMODE.FCStd = doc fcstd_f5c4d4c8f7ee ----
FCSTD DOCUMENT  (FreeCAD 1.0R39319 (Git))
Label: PLASTIC-MAPMODE
License: All rights reserved
LicenseURL: https://en.wikipedia.org/wiki/All_rights_reserved
objects: Sketcher::SketchObject×2, PartDesign::Revolution×1, PartDesign::CoordinateSystem×1, PartDesign::Pocket×1, PartDesign::Body×1
note: 12 computed .brp shape members not serialized (recipe doc carries the construction recipe); baked Part::Feature solids carry a one-line shape summary decoded from their .brp

FEATURE [Sketcher::SketchObject] Sketch
  ArcFitTolerance = 1e-06
  AttachmentSupport = -> [XZ_Plane]
  FullyConstrained = true
  MakeInternals = false
  MapMode = 5
  Placement = pos=(0,0,0) rot=(1,0,0;1.5708rad)
  sketch-geometry (19):
    g0: LineSegment StartX=0 StartY=0 StartZ=0 EndX=0 EndY=1.51132 EndZ=0
    g1: LineSegment StartX=-0.5 StartY=1.8 StartZ=0 EndX=-1.68 EndY=1.8 EndZ=0
    g2: LineSegment StartX=-1.78 StartY=1.7 StartZ=0 EndX=-1.78 EndY=0.85 EndZ=0
    g3: LineSegment StartX=-1.78 StartY=0.85 StartZ=0 EndX=-2.93 EndY=0.85 EndZ=0
    g4: LineSegment StartX=-3.03 StartY=1.8 StartZ=0 EndX=-4.21 EndY=1.8 EndZ=0
    g5: LineSegment StartX=-4.71 StartY=1.51132 StartZ=0 EndX=-4.71 EndY=0 EndZ=0
    g6: LineSegment StartX=-4.71 StartY=0 StartZ=0 EndX=0 EndY=0 EndZ=0
    g7: LineSegment StartX=-4.71 StartY=1.51132 StartZ=0 EndX=-4.21 EndY=1.8 EndZ=0
    g8: LineSegment StartX=-2.93 StartY=0.85 StartZ=0 EndX=-2.93 EndY=1.7 EndZ=0
    g9: LineSegment StartX=-3.03 StartY=1.8 StartZ=0 EndX=-2.93 EndY=1.7 EndZ=0
    g10: LineSegment StartX=-1.68 StartY=1.8 StartZ=0 EndX=-1.78 EndY=1.7 EndZ=0
    g11: LineSegment [constr] StartX=-2.855 StartY=0 StartZ=0 EndX=-1.855 EndY=0 EndZ=0
    g12: LineSegment [constr] StartX=-1.855 StartY=0 StartZ=0 EndX=-1.855 EndY=1.8 EndZ=0
    g13: LineSegment [constr] StartX=-1.855 StartY=1.8 StartZ=0 EndX=-2.855 EndY=1.8 EndZ=0
    g14: LineSegment [constr] StartX=-2.855 StartY=1.8 StartZ=0 EndX=-2.855 EndY=0 EndZ=0
    g15: LineSegment [constr] StartX=-2.93 StartY=0.85 StartZ=0 EndX=-2.855 EndY=0 EndZ=0
    g16: LineSegment [constr] StartX=-1.855 StartY=0 StartZ=0 EndX=-1.78 EndY=0.85 EndZ=0
    g17: GeomPoint [constr] X=0 Y=1.8 Z=0
    g18: LineSegment StartX=0 StartY=1.51132 StartZ=0 EndX=-0.5 EndY=1.8 EndZ=0
  constraints (57):
    c: Coincident(g0,g-1)
    c: PointOnObject(g17,g-2)
    c: Horizontal(g1)
    c: Vertical(g2)
    c: Coincident(g3,g2)
    c: Horizontal(g3)
    c: Horizontal(g4)
    c: Vertical(g5)
    c: Coincident(g6,g5)
    c: Coincident(g6,g0)
    c: Horizontal(g6)
    c: DistanceY(g0,g3) = 0.85
    c: Coincident(g4,g7)
    c: Coincident(g5,g7)
    c: DistanceX(g3,g3) = 1.15
    c: DistanceY(g0,g17) = 1.8
    c: Coincident(g8,g3)
    c: Vertical(g8)
    c: Equal(g9,g10)
    c: Angle(g4,g9) = 2.35619
    c: Angle(g10,g1) = 2.35619
    c: Coincident(g4,g9)
    c: Coincident(g8,g9)
    c: Coincident(g2,g10)
    c: Coincident(g1,g10)
    c: DistanceY(g5,g4) = 1.8
    c: Coincident(g11,g12)
    c: Coincident(g12,g13)
    c: Coincident(g13,g14)
    c: Coincident(g14,g11)
    c: Horizontal(g11)
    c: Horizontal(g13)
    c: Vertical(g12)
    c: Vertical(g14)
    c: PointOnObject(g11,g6)
    c: DistanceX(g13,g13) = 1
    c: DistanceX(g12,g2) = 0.075
    c: DistanceX(g8,g13) = 0.075
    c: Coincident(g15,g3)
    c: Coincident(g15,g11)
    c: Coincident(g16,g11)
    c: Coincident(g16,g2)
    c: Equal(g16,g15)
    c: PointOnObject(g17,g0)
    c: PointOnObject(g17,g1)
    c: Coincident(g18,g0)
    c: Coincident(g18,g1)
    c: DistanceX(g6,g6) = 4.71
    c: PointOnObject(g12,g1)
    c: Distance(g0,g2) = 1.78
    c: Distance(g8,g5) = 1.78
    c: Distance(g8,g5) = 1.78
    c: DistanceX(g18,g18) = 0.5
    c: Angle(g1,g18) = 2.61799
    c: Equal(g7,g18)
    c: Angle(g7,g4) = 2.61799
    c: DistanceX(g9,g9) = 0.1
FEATURE [PartDesign::Revolution] Revolution
  Angle = 360
  Angle2 = 60
  Axis = (1,0,0)
  Base = (0,0,0)
  Placement = pos=(0,0,0) rot=(1,0,0;1.5708rad)
  Profile = -> Sketch
  ReferenceAxis = -> Sketch [H_Axis]
  Refine = true
  Suppressed = false
  Type = 0
FEATURE [Sketcher::SketchObject] Sketch001
  ArcFitTolerance = 1e-06
  AttachmentSupport = -> [XY_Plane]
  FullyConstrained = true
  MakeInternals = false
  MapMode = 5
  sketch-geometry (4):
    g0: LineSegment StartX=-6 StartY=-1.7 StartZ=0 EndX=-6 EndY=-3.7 EndZ=0
    g1: LineSegment StartX=-6 StartY=-3.7 StartZ=0 EndX=0 EndY=-3.7 EndZ=0
    g2: LineSegment StartX=0 StartY=-3.7 StartZ=0 EndX=0 EndY=-1.7 EndZ=0
    g3: LineSegment StartX=0 StartY=-1.7 StartZ=0 EndX=-6 EndY=-1.7 EndZ=0
  constraints (12):
    c: Coincident(g0,g1)
    c: Coincident(g1,g2)
    c: Coincident(g2,g3)
    c: Coincident(g3,g0)
    c: Vertical(g0)
    c: Vertical(g2)
    c: Horizontal(g1)
    c: Horizontal(g3)
    c: PointOnObject(g1,g-2)
    c: DistanceY(g2,g2) = 2
    c: DistanceY(g2,g-1) = 1.7
    c: DistanceX(g3,g3) = 6
FEATURE [PartDesign::CoordinateSystem] LCS_1
  AttacherType = Attacher::AttachEngine3D
  MapMode = 45
  Placement = pos=(-2.35,1e-16,-4e-16) rot=(0.57735,0.57735,0.57735;2.0944rad)
FEATURE [PartDesign::Pocket] Pocket
  BaseFeature = -> Revolution
  Direction = (0,0,-1)
  Length = 10
  Length2 = 5
  Midplane = true
  Placement = pos=(0,0,0) rot=(1,0,0;1.5708rad)
  Profile = -> Sketch001
  ReferenceAxis = -> Sketch001 [N_Axis]
  Refine = true
  Suppressed = false
  Type = 0
FEATURE [PartDesign::Body] Body  label="PLASTIC-MAPMODE"
  AllowCompound = false
  Group = -> [Sketch,Revolution,Sketch001,LCS_1,Pocket]
  Origin = -> Origin
  Tip = -> Pocket
---- part ../Design/RUBBER-FOOT/RUBBER-FOOT.FCStd = doc fcstd_b985480773ca ----
FCSTD DOCUMENT  (FreeCAD 1.0R39285 (Git))
Label: RUBBER-FOOT
License: All rights reserved
LicenseURL: https://en.wikipedia.org/wiki/All_rights_reserved
objects: TechDraw::DrawViewDimension×7, TechDraw::DrawViewPart×3, TechDraw::DrawHatch×3, PartDesign::Line×2, Sketcher::SketchObject×1, PartDesign::Pad×1, TechDraw::DrawSVGTemplate×1, TechDraw::DrawViewAnnotation×1, PartDesign::Plane×1, PartDesign::Body×1, TechDraw::DrawPage×1
note: 19 computed .brp shape members not serialized (recipe doc carries the construction recipe); baked Part::Feature solids carry a one-line shape summary decoded from their .brp

FEATURE [Sketcher::SketchObject] Sketch
  ArcFitTolerance = 0
  AttachmentSupport = -> [XY_Plane]
  FullyConstrained = true
  MakeInternals = false
  MapMode = 5
  sketch-geometry (10):
    g0: LineSegment StartX=-4.15 StartY=4.15 StartZ=0 EndX=-2.15 EndY=4.15 EndZ=0
    g1: LineSegment StartX=-2.15 StartY=11.85 StartZ=0 EndX=-8.15 EndY=11.85 EndZ=0
    g2: LineSegment StartX=-16 StartY=4 StartZ=0 EndX=-16 EndY=-2 EndZ=0
    g3: LineSegment StartX=-8.3 StartY=-7e-16 StartZ=0 EndX=-8.3 EndY=-2 EndZ=0
    g4: ArcOfCircle CenterX=-8.15 CenterY=4 CenterZ=0 NormalX=0 NormalY=0 NormalZ=1 AngleXU=0 Radius=7.85 StartAngle=1.5708 EndAngle=3.14159
    g5: ArcOfCircle CenterX=-4.15 CenterY=1.8645e-10 CenterZ=0 NormalX=0 NormalY=0 NormalZ=1 AngleXU=0 Radius=4.15 StartAngle=1.5708 EndAngle=3.14159
    g6: ArcOfCircle CenterX=-12.15 CenterY=-2 CenterZ=0 NormalX=0 NormalY=0 NormalZ=1 AngleXU=0 Radius=3.85 StartAngle=3.14159 EndAngle=6.28319
    g7: ArcOfCircle CenterX=-2.15 CenterY=8 CenterZ=0 NormalX=0 NormalY=0 NormalZ=1 AngleXU=0 Radius=3.85 StartAngle=4.71239 EndAngle=7.85398
    g8: GeomPoint [constr] X=1.7 Y=8 Z=0
    g9: GeomPoint [constr] X=-12.15 Y=-5.85 Z=0
  constraints (24):
    c: Horizontal(g0)
    c: Horizontal(g1)
    c: Vertical(g2)
    c: Tangent(g1,g4) = -1.5708
    c: Tangent(g2,g4) = -1.5708
    c: Tangent(g0,g5) = 1.5708
    c: Tangent(g3,g5) = -1.5708
    c: DistanceX(g2,g3) = 7.7
    c: Radius(g4) = 7.85
    c: Vertical(g3)
    c: Radius(g5) = 4.15
    c: Tangent(g7,g1) = -1.5708
    c: Tangent(g7,g0) = -1.5708
    c: Tangent(g6,g3) = 1.5708
    c: Tangent(g6,g2) = -1.5708
    c: PointOnObject(g8,g7)
    c: Horizontal(g7,g8)
    c: PointOnObject(g9,g6)
    c: Vertical(g6,g9)
    c: DistanceY(g9,g1) = 17.7
    c: DistanceX(g2,g8) = 17.7
    c: Radius(g7) = 3.85
    c: PointOnObject(g-1,g5)
    c: Horizontal(g-1,g3)
FEATURE [PartDesign::Pad] Pad
  Direction = (0,0,1)
  Length = 1
  Length2 = 10
  Profile = -> Sketch
  ReferenceAxis = -> Sketch [N_Axis]
  Suppressed = false
  Type = 0
FEATURE [TechDraw::DrawSVGTemplate] Template
  EditableTexts = COLOR=Black - RAL code: 9004; CreationDate=2023/12/07; E.G.APPROVED=APPROVED; FC-Scale=5:1; FC-Title=RUBBER-FOOT; IntechStudioLtd.=Intech Studio Ltd.; MATERIAL=Silicon or rubber; REV=02; STANDARD=DIN 16742-TG4
  Height = 297
  Orientation = 1
  Template = <userpath>/Desktop/A3_LandscapeTD_MODIFIED.svg
  Width = 420
FEATURE [TechDraw::DrawViewAnnotation] Annotation
  Font = osifont
  LineSpace = 100
  LockPosition = false
  MaxWidth = -1
  Rotation = 0
  ScaleType = 0
  Text = Self-adhesive on one side | Other side is aesthetical
  TextSize = 5
  TextStyle = 0
  X = 113.346
  Y = 98.3157
FEATURE [PartDesign::Plane] Plane_1
  AttachmentSupport = -> [Pad]
  Length = 100
  ResizeMode = 1
  Width = 100
FEATURE [PartDesign::Line] CircleAxis_1
  AttacherType = Attacher::AttachEngineLine
  AttachmentSupport = -> [Pad]
  Length = 17.1927
  MapMode = 19
  Placement = pos=(-2.15,8,1) rot=(0,0,-1;1.5708rad)
  ResizeMode = 1
FEATURE [PartDesign::Line] CircleAxis_2
  AttacherType = Attacher::AttachEngineLine
  AttachmentSupport = -> [Pad]
  Length = 17.1927
  MapMode = 19
  Placement = pos=(-12.15,-2,1) rot=(0,0,1;3.14159rad)
  ResizeMode = 1
FEATURE [PartDesign::Body] Body  label="RUBBER-FOOT"
  AllowCompound = false
  Group = -> [Sketch,Pad,Plane_1,CircleAxis_1,CircleAxis_2]
  Origin = -> Origin
  Tip = -> Pad
FEATURE [TechDraw::DrawViewPart] View
  CoarseView = false
  Direction = (0,0,1)
  Focus = 100
  HardHidden = true
  IsoCount = 0
  IsoHidden = false
  IsoVisible = false
  LockPosition = false
  Perspective = false
  Rotation = 0
  Scale = 5
  ScaleType = 2
  ScrubCount = 0
  SeamHidden = false
  SeamVisible = true
  SmoothHidden = false
  SmoothVisible = true
  Source = -> [Body]
  X = 117.879
  XDirection = (1,0,0)
  Y = 186.048
FEATURE [TechDraw::DrawViewPart] View001
  CoarseView = false
  Direction = (-1,0,0)
  Focus = 100
  HardHidden = true
  IsoCount = 0
  IsoHidden = false
  IsoVisible = false
  LockPosition = false
  Perspective = false
  Rotation = 0
  Scale = 5
  ScaleType = 2
  ScrubCount = 0
  SeamHidden = false
  SeamVisible = true
  SmoothHidden = false
  SmoothVisible = true
  Source = -> [Body]
  X = 261.925
  XDirection = (0,0,1)
  Y = 188.134
FEATURE [TechDraw::DrawViewPart] View002
  CoarseView = false
  Direction = (0.57735,0.57735,0.57735)
  Focus = 100
  HardHidden = true
  IsoCount = 0
  IsoHidden = false
  IsoVisible = false
  LockPosition = false
  Perspective = false
  Rotation = 0
  Scale = 5
  ScaleType = 2
  ScrubCount = 0
  SeamHidden = false
  SeamVisible = true
  SmoothHidden = false
  SmoothVisible = true
  Source = -> [Body]
  X = 364.506
  XDirection = (0.707107,0,-0.707107)
  Y = 231.154
FEATURE [TechDraw::DrawHatch] Hatch  label="HatchF1"
  HatchPattern = C:/Program Files/FreeCAD 0.21/data/Mod/TechDraw/Patterns/solid.svg
  Source = -> View002 [Face1]
FEATURE [TechDraw::DrawHatch] Hatch001  label="Hatch001F4"
  HatchPattern = C:/Program Files/FreeCAD 0.21/data/Mod/TechDraw/Patterns/solid.svg
  Source = -> View002 [Face4]
FEATURE [TechDraw::DrawHatch] Hatch002  label="Hatch002F3"
  HatchPattern = C:/Program Files/FreeCAD 0.21/data/Mod/TechDraw/Patterns/solid.svg
  Source = -> View002 [Face3,Face2,Face6,Face7,Face5]
FEATURE [TechDraw::DrawViewDimension] Dimension
  AngleOverride = false
  Arbitrary = false
  ArbitraryTolerances = false
  EqualTolerance = false
  ExtensionAngle = 0
  FormatSpec = %.2w
  FormatSpecOverTolerance = %+.2w
  FormatSpecUnderTolerance = %+.2w
  Inverted = false
  LineAngle = 0
  LockPosition = false
  MeasureType = 1
  OverTolerance = 0
  References2D = -> [View]
  Rotation = 0
  ScaleType = 0
  TheoreticalExact = false
  Type = 1
  UnderTolerance = -0.5
  X = -0.788548
  Y = 62.3415
FEATURE [TechDraw::DrawViewDimension] Dimension001
  AngleOverride = false
  Arbitrary = false
  ArbitraryTolerances = false
  EqualTolerance = false
  ExtensionAngle = 0
  FormatSpec = %.2w
  FormatSpecOverTolerance = %+.2w
  FormatSpecUnderTolerance = %+.2w
  Inverted = false
  LineAngle = 0
  LockPosition = false
  MeasureType = 1
  OverTolerance = 0
  References2D = -> [View]
  Rotation = 0
  ScaleType = 0
  TheoreticalExact = false
  Type = 2
  UnderTolerance = -0.5
  X = -65.1003
  Y = 3.4233
FEATURE [TechDraw::DrawViewDimension] Dimension002
  AngleOverride = false
  Arbitrary = false
  ArbitraryTolerances = false
  EqualTolerance = true
  ExtensionAngle = 0
  FormatSpec = R%.2w
  FormatSpecOverTolerance = %+.2w
  FormatSpecUnderTolerance = %+.2w
  Inverted = false
  LineAngle = 0
  LockPosition = false
  MeasureType = 1
  OverTolerance = 0
  References2D = -> [View]
  Rotation = 0
  ScaleType = 0
  TheoreticalExact = false
  Type = 4
  UnderTolerance = 0
  X = 8.94427
  Y = -2.89374
FEATURE [TechDraw::DrawViewDimension] Dimension003
  AngleOverride = false
  Arbitrary = false
  ArbitraryTolerances = false
  EqualTolerance = true
  ExtensionAngle = 0
  FormatSpec = R%.2w
  FormatSpecOverTolerance = %+.2w
  FormatSpecUnderTolerance = %+.2w
  Inverted = false
  LineAngle = 0
  LockPosition = false
  MeasureType = 1
  OverTolerance = 0
  References2D = -> [View]
  Rotation = 0
  ScaleType = 0
  TheoreticalExact = false
  Type = 4
  UnderTolerance = 0
  X = -56.5573
  Y = 68.9744
FEATURE [TechDraw::DrawViewDimension] Dimension004
  AngleOverride = false
  Arbitrary = false
  ArbitraryTolerances = false
  EqualTolerance = true
  ExtensionAngle = 0
  FormatSpec = 2x R%.2w
  FormatSpecOverTolerance = %+.2w
  FormatSpecUnderTolerance = %+.2w
  Inverted = false
  LineAngle = 0
  LockPosition = false
  MeasureType = 1
  OverTolerance = 0
  References2D = -> [View]
  Rotation = 0
  ScaleType = 0
  TheoreticalExact = false
  Type = 4
  UnderTolerance = 0
  X = 63.0908
  Y = 42.9779
FEATURE [TechDraw::DrawViewDimension] Dimension005
  AngleOverride = false
  Arbitrary = false
  ArbitraryTolerances = false
  EqualTolerance = false
  ExtensionAngle = 0
  FormatSpec = 2x %.2w
  FormatSpecOverTolerance = %+.2w
  FormatSpecUnderTolerance = %+.2w
  Inverted = false
  LineAngle = 0
  LockPosition = false
  MeasureType = 1
  OverTolerance = 0
  References2D = -> [View]
  Rotation = 0
  ScaleType = 0
  TheoreticalExact = false
  Type = 1
  UnderTolerance = -0.5
  X = -25
  Y = -58.5708
FEATURE [TechDraw::DrawViewDimension] Dimension006
  AngleOverride = false
  Arbitrary = false
  ArbitraryTolerances = false
  EqualTolerance = true
  ExtensionAngle = 0
  FormatSpec = %.2w
  FormatSpecOverTolerance = %+.2w
  FormatSpecUnderTolerance = %+.2w
  Inverted = false
  LineAngle = 0
  LockPosition = false
  MeasureType = 1
  OverTolerance = 0
  References2D = -> [View001]
  Rotation = 0
  ScaleType = 0
  TheoreticalExact = false
  Type = 1
  UnderTolerance = 0
  X = 8.85411
  Y = 61.7117
FEATURE [TechDraw::DrawPage] Page  label="RUBBER-FOOT_Drawing"
  KeepUpdated = true
  NextBalloonIndex = 3
  ProjectionType = 0
  Template = -> Template
  Views = -> [View,View001,View002,Dimension,Dimension001,Dimension002,Dimension003,Dimension004,Dimension005,Dimension006,Annotation]
